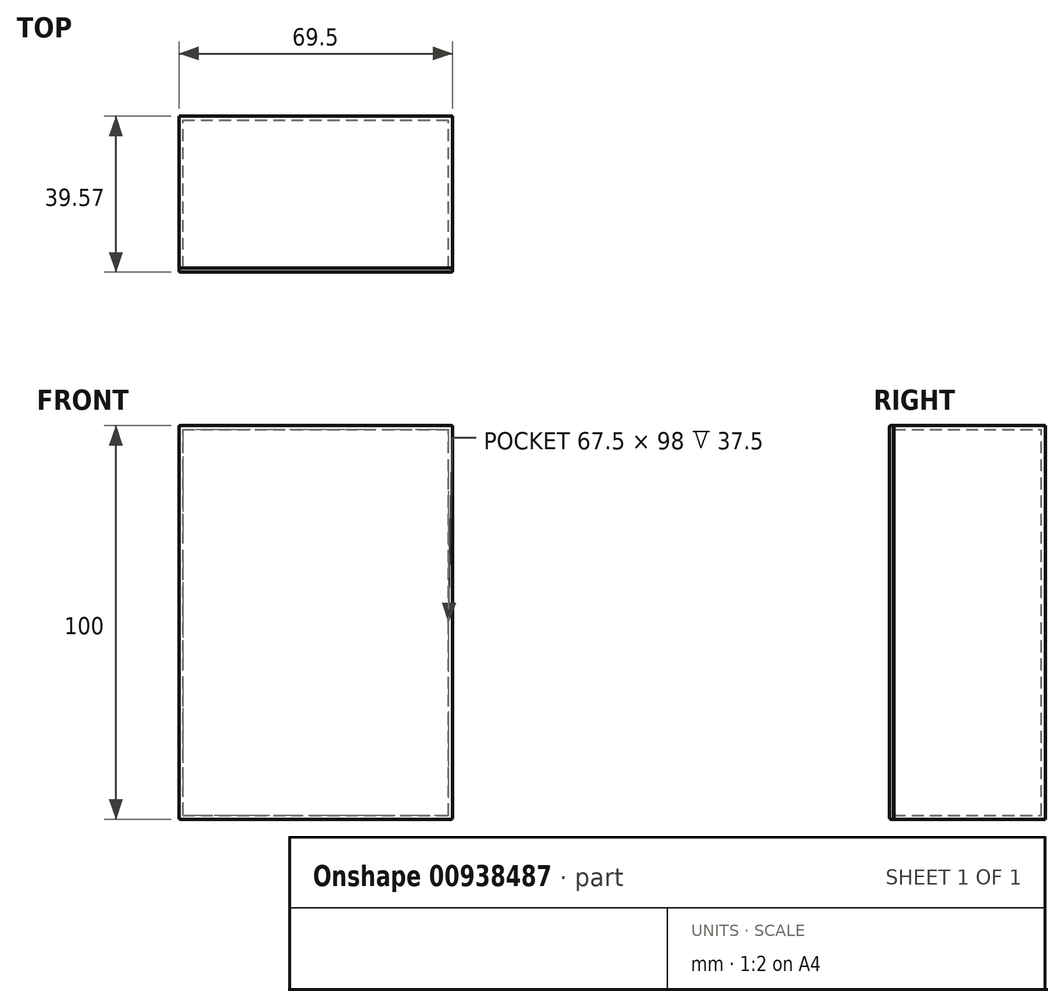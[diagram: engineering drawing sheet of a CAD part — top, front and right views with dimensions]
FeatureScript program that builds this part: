
annotation { "Feature Type Name" : "Feature", "Feature Type Description" : "" }
export const myFeature = defineFeature(function(context is Context, id is Id, definition is map)
    precondition{}
    {
        {
            var Q0;
            Q0=qCreatedBy(makeId("Front.planeOp"),FACE);
            var sketch = newSketch(context, id + "F0", { "sketchPlane" : qUnion([Q0])});
            skLineSegment(sketch, "E0.bottom", {"start": v(13.44, 0) * mm, "end": v(82.94, 0) * mm});
            skLineSegment(sketch, "E0.top", {"start": v(13.44, 100) * mm, "end": v(82.94, 100) * mm});
            skLineSegment(sketch, "E0.left", {"start": v(13.44, 0) * mm, "end": v(13.44, 100) * mm});
            skLineSegment(sketch, "E0.right", {"start": v(82.94, 0) * mm, "end": v(82.94, 100) * mm});
            skSolve(sketch);
        }
        {
            var Q0;
            Q0 = qSketchRegion(id + "F0", true);
            extrude(context, id + "F1", {"entities" : qUnion([Q0]), "depth" : 39.5 * mm, "offsetDistance" : 25 * mm});
        }
        {
            var Q0;
            Q0=makeQuery(id+"F1.opExtrude","CAP_FACE",FACE,{"disambiguationData":[OSD([sQuery(id+"F0.wireOp",EDGE,"E0.bottom"),sQuery(id+"F0.wireOp",EDGE,"E0.top"),sQuery(id+"F0.wireOp",EDGE,"E0.left"),sQuery(id+"F0.wireOp",EDGE,"E0.right")])],"isStart":true});
            extrude(context, id + "F2", {"entities" : qUnion([Q0]), "operationType" : NewBodyOperationType.REMOVE, "oppositeDirection" : true, "depth" : 1 * mm, "offsetDistance" : 25 * mm});
        }
        {
            var Q0;
            Q0=makeQuery(id+"F1.opExtrude","CAP_FACE",FACE,{"disambiguationData":[OSD([sQuery(id+"F0.wireOp",EDGE,"E0.bottom"),sQuery(id+"F0.wireOp",EDGE,"E0.top"),sQuery(id+"F0.wireOp",EDGE,"E0.left"),sQuery(id+"F0.wireOp",EDGE,"E0.right")])],"isStart":false});
            shell(context, id + "F3", {"entities" : qUnion([Q0]), "thickness" : 1 * mm});
        }
        {
            var Q0;
            Q0=qCreatedBy(makeId("Top.planeOp"),FACE);
            var sketch = newSketch(context, id + "F4", { "sketchPlane" : qUnion([Q0])});
            skLineSegment(sketch, "E1.bottom", {"start": v(13.44, -39.57) * mm, "end": v(82.94, -39.57) * mm});
            skLineSegment(sketch, "E1.top", {"start": v(13.44, -40.57) * mm, "end": v(82.94, -40.57) * mm});
            skLineSegment(sketch, "E1.left", {"start": v(13.44, -39.57) * mm, "end": v(13.44, -40.57) * mm});
            skLineSegment(sketch, "E1.right", {"start": v(82.94, -39.57) * mm, "end": v(82.94, -40.57) * mm});
            skSolve(sketch);
        }
        {
            var Q0;
            Q0 = qSketchRegion(id + "F4", true);
            extrude(context, id + "F5", {"entities" : qUnion([Q0]), "depth" : 100 * mm, "offsetDistance" : 25 * mm});
        }
        {
            var Q0;
            Q0=makeQuery(id+"F1.opExtrude","SWEPT_EDGE",EDGE,{"disambiguationData":[OSD([sQuery(id+"F0.wireOp",EDGE,"E0.top"),sQuery(id+"F0.wireOp",EDGE,"E0.right")])]});
            fillet(context, id + "F6", {"entities" : qUnion([Q0]), "tangentPropagation" : true, "radius" : 0.3 * mm, "defaultsChanged" : true, "vertexSettings" : [], "allowEdgeOverflow" : false});
        }
        {
            var Q0;
            Q0=makeQuery(id+"F2.boolean.opBoolean","COPY",EDGE,{"derivedFrom":makeQuery(id+"F2.opExtrude","CAP_EDGE",EDGE,{"disambiguationData":[OSD([sQuery(id+"F0.wireOp",EDGE,"E0.top")])],"isStart":false})});
            var Q1;
            Q1=makeQuery(id+"F1.opExtrude","SWEPT_EDGE",EDGE,{"disambiguationData":[OSD([sQuery(id+"F0.wireOp",EDGE,"E0.top"),sQuery(id+"F0.wireOp",EDGE,"E0.left")])]});
            var Q2;
            Q2=makeQuery(id+"F2.boolean.opBoolean","COPY",EDGE,{"derivedFrom":makeQuery(id+"F2.opExtrude","CAP_EDGE",EDGE,{"disambiguationData":[OSD([sQuery(id+"F0.wireOp",EDGE,"E0.left")])],"isStart":false})});
            var Q3;
            Q3=makeQuery(id+"F5.opExtrude","CAP_EDGE",EDGE,{"disambiguationData":[OSD([sQuery(id+"F4.wireOp",EDGE,"E1.top")])],"isStart":false});
            var Q4;
            Q4=makeQuery(id+"F5.opExtrude","SWEPT_EDGE",EDGE,{"disambiguationData":[OSD([sQuery(id+"F4.wireOp",EDGE,"E1.top"),sQuery(id+"F4.wireOp",EDGE,"E1.left")])]});
            var Q5;
            Q5=makeQuery(id+"F5.opExtrude","CAP_EDGE",EDGE,{"disambiguationData":[OSD([sQuery(id+"F4.wireOp",EDGE,"E1.left")])],"isStart":false});
            var Q6;
            Q6=makeQuery(id+"F5.opExtrude","CAP_EDGE",EDGE,{"disambiguationData":[OSD([sQuery(id+"F4.wireOp",EDGE,"E1.right")])],"isStart":false});
            var Q7;
            Q7=makeQuery(id+"F5.opExtrude","SWEPT_EDGE",EDGE,{"disambiguationData":[OSD([sQuery(id+"F4.wireOp",EDGE,"E1.top"),sQuery(id+"F4.wireOp",EDGE,"E1.right")])]});
            var Q8;
            Q8=makeQuery(id+"F1.opExtrude","SWEPT_EDGE",EDGE,{"disambiguationData":[OSD([sQuery(id+"F0.wireOp",EDGE,"E0.bottom"),sQuery(id+"F0.wireOp",EDGE,"E0.right")])]});
            var Q9;
            Q9=makeQuery(id+"F5.opExtrude","CAP_EDGE",EDGE,{"disambiguationData":[OSD([sQuery(id+"F4.wireOp",EDGE,"E1.top")])],"isStart":true});
            var Q10;
            Q10=makeQuery(id+"F5.opExtrude","CAP_EDGE",EDGE,{"disambiguationData":[OSD([sQuery(id+"F4.wireOp",EDGE,"E1.right")])],"isStart":true});
            var Q11;
            Q11=makeQuery(id+"F5.opExtrude","CAP_EDGE",EDGE,{"disambiguationData":[OSD([sQuery(id+"F4.wireOp",EDGE,"E1.left")])],"isStart":true});
            var Q12;
            Q12=makeQuery(id+"F1.opExtrude","SWEPT_EDGE",EDGE,{"disambiguationData":[OSD([sQuery(id+"F0.wireOp",EDGE,"E0.bottom"),sQuery(id+"F0.wireOp",EDGE,"E0.left")])]});
            var Q13;
            Q13=makeQuery(id+"F2.boolean.opBoolean","COPY",EDGE,{"derivedFrom":makeQuery(id+"F2.opExtrude","CAP_EDGE",EDGE,{"disambiguationData":[OSD([sQuery(id+"F0.wireOp",EDGE,"E0.bottom")])],"isStart":false})});
            var Q14;
            Q14=makeQuery(id+"F2.boolean.opBoolean","COPY",EDGE,{"derivedFrom":makeQuery(id+"F2.opExtrude","CAP_EDGE",EDGE,{"disambiguationData":[OSD([sQuery(id+"F0.wireOp",EDGE,"E0.right")])],"isStart":false})});
            fillet(context, id + "F7", {"entities" : qUnion([Q0, Q1, Q2, Q3, Q4, Q5, Q6, Q7, Q8, Q9, Q10, Q11, Q12, Q13, Q14]), "tangentPropagation" : true, "radius" : 0.3 * mm, "defaultsChanged" : true, "vertexSettings" : [], "allowEdgeOverflow" : false});
        }
    });
